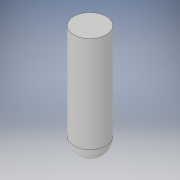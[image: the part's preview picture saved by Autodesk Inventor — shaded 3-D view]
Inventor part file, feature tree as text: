
AUTODESK INVENTOR PART (.ipt)
format: ipt  version: 2019.4 (Build 234330000, 330)  size: 105,472 bytes
history: native  units: in
note: dims shown in document units (in); Inventor stores cm internally (conversion verified against a paired STEP export)
features: extrude x1, fillet x1, sketch x1
ambient origin geometry x8: Origin, YZ Plane, XZ Plane, XY Plane, X Axis, Y Axis, Z Axis, Center Point
bodies: Solid1 (feature_tree)
feature tree (3):
  extrude  "Extrusion1"  Depth=4.5in TaperAngle=0.0deg
  fillet  "Fillet1"  Radius=0.125in
  sketch  "Sketch1"  dims[d0=1.3in d1=4.5in d2=0.0in d3=0.125in d4=0.125in d5=0.625in d6=0.2149in]
